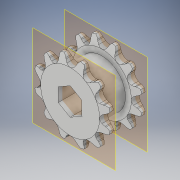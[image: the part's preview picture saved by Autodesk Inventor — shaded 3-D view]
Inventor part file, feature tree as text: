
AUTODESK INVENTOR PART (.ipt)
format: ipt  version: 2017 (Build 210142000, 142)  size: 601,088 bytes
history: native  units: in
note: dims shown in document units (in); Inventor stores cm internally (conversion verified against a paired STEP export)
features: plane x2, other x1
ambient origin geometry x8: Origin, YZ Plane, XZ Plane, XY Plane, X Axis, Y Axis, Z Axis, Center Point
bodies: Solid1 (feature_tree)
feature tree (3):
  plane  "Work Plane1"
  plane  "Work Plane2"
  other  "Cut-Extrude3"
